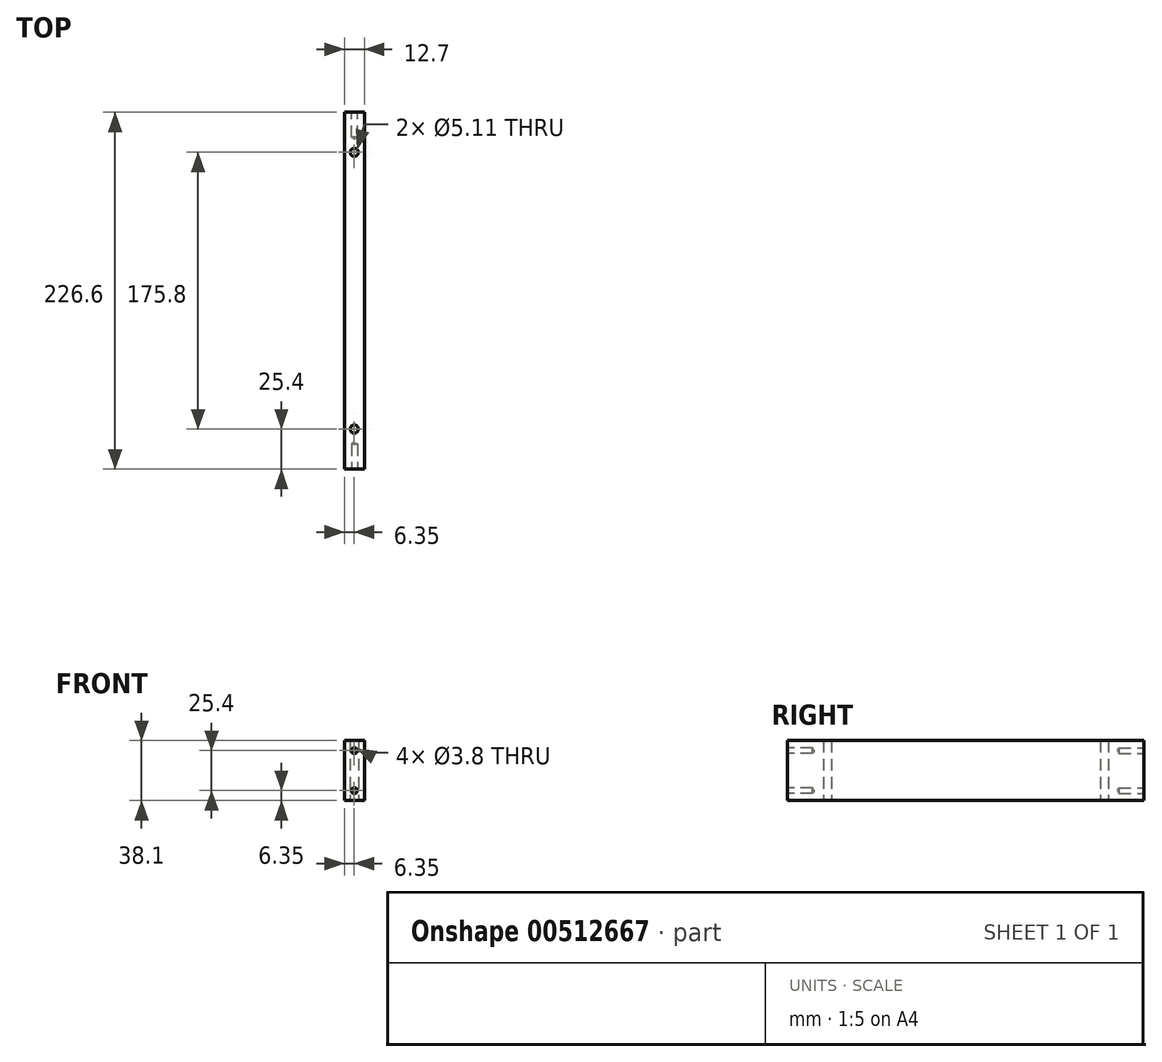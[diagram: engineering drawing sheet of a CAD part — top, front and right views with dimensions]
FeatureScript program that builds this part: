
annotation { "Feature Type Name" : "Feature", "Feature Type Description" : "" }
export const myFeature = defineFeature(function(context is Context, id is Id, definition is map)
    precondition{}
    {
        {
            var Q0;
            Q0=qCreatedBy(makeId("Front.planeOp"),FACE);
            var sketch = newSketch(context, id + "F0", { "sketchPlane" : qUnion([Q0])});
            skLineSegment(sketch, "E0.bottom", {"start": v(0, 0) * mm, "end": v(12.7, 0) * mm});
            skLineSegment(sketch, "E0.top", {"start": v(0, 38.1) * mm, "end": v(12.7, 38.1) * mm});
            skLineSegment(sketch, "E0.left", {"start": v(0, 0) * mm, "end": v(0, 38.1) * mm});
            skLineSegment(sketch, "E0.right", {"start": v(12.7, 0) * mm, "end": v(12.7, 38.1) * mm});
            skSolve(sketch);
        }
        {
            var Q0;
            Q0 = qSketchRegion(id + "F0", true);
            extrude(context, id + "F1", {"entities" : qUnion([Q0]), "depth" : 252 * mm - 25.4 * mm});
        }
        {
            var Q0;
            Q0=makeQuery(id+"F1.opExtrude","CAP_FACE",FACE,{"disambiguationData":[OSD([sQuery(id+"F0.wireOp",EDGE,"E0.bottom"),sQuery(id+"F0.wireOp",EDGE,"E0.top"),sQuery(id+"F0.wireOp",EDGE,"E0.left"),sQuery(id+"F0.wireOp",EDGE,"E0.right")])],"isStart":false});
            var sketch = newSketch(context, id + "F2", { "sketchPlane" : qUnion([Q0])});
            skLineSegment(sketch, "E1", {"start": v(0, 38.1) * mm, "end": v(6.35, 38.1) * mm});
            skLineSegment(sketch, "E2", {"start": v(6.35, 38.1) * mm, "end": v(6.35, 31.75) * mm});
            skLineSegment(sketch, "E3", {"start": v(6.35, 0) * mm, "end": v(6.35, 6.35) * mm});
            skSolve(sketch);
        }
        {
            var Q0;
            Q0=sQuery(id+"F2.wireOp",VERTEX,"E2.end");
            var Q1;
            Q1=sQuery(id+"F2.wireOp",VERTEX,"E3.end");
            var Q2;
            Q2=makeQuery(id+"F1.opExtrude","SWEPT_BODY",BODY,{"disambiguationData":[OSD([sQuery(id+"F0.wireOp",EDGE,"E0.bottom"),sQuery(id+"F0.wireOp",EDGE,"E0.top"),sQuery(id+"F0.wireOp",EDGE,"E0.left"),sQuery(id+"F0.wireOp",EDGE,"E0.right")])]});
            hole(context, id + "F3", {"style" : HoleStyle.SIMPLE, "endStyle" : HoleEndStyle.BLIND, "standardTappedOrClearance" : lookupTablePath({ "standard" : "ANSI", "engagement" : "75%", "pitch" : "24 tpi", "size" : "#10", "type" : "Tapped" }), "standardBlindInLast" : lookupTablePath({ "standard" : "ANSI", "engagement" : "75%", "pitch" : "24 tpi", "size" : "#10", "type" : "Tapped" }), "holeDiameter" : 3.8 * mm, "showTappedDepth" : true, "holeDepth" : 15.88 * mm, "isTappedThrough" : true, "tappedDepth" : 12.7 * mm, "tapClearance" : 3, "locations" : qUnion([Q0, Q1]), "scope" : qUnion([Q2]), "majorDiameter" : 4.83 * mm});
        }
        {
            var Q0;
            Q0=makeQuery(id+"F1.opExtrude","CAP_FACE",FACE,{"disambiguationData":[OSD([sQuery(id+"F0.wireOp",EDGE,"E0.bottom"),sQuery(id+"F0.wireOp",EDGE,"E0.top"),sQuery(id+"F0.wireOp",EDGE,"E0.left"),sQuery(id+"F0.wireOp",EDGE,"E0.right")])],"isStart":true});
            var sketch = newSketch(context, id + "F4", { "sketchPlane" : qUnion([Q0])});
            skLineSegment(sketch, "E4", {"start": v(-6.35, 38.1) * mm, "end": v(-6.35, 31.75) * mm});
            skPoint(sketch, "E4.endSnap0", {"position": v(-6.35, 38.1) * mm});
            skLineSegment(sketch, "E5", {"start": v(-6.35, 0) * mm, "end": v(-6.35, 6.35) * mm});
            skSolve(sketch);
        }
        {
            var Q0;
            Q0=sQuery(id+"F4.wireOp",VERTEX,"E4.end");
            var Q1;
            Q1=sQuery(id+"F4.wireOp",VERTEX,"E5.end");
            var Q2;
            Q2=makeQuery(id+"F1.opExtrude","SWEPT_BODY",BODY,{"disambiguationData":[OSD([sQuery(id+"F0.wireOp",EDGE,"E0.bottom"),sQuery(id+"F0.wireOp",EDGE,"E0.top"),sQuery(id+"F0.wireOp",EDGE,"E0.left"),sQuery(id+"F0.wireOp",EDGE,"E0.right")])]});
            hole(context, id + "F5", {"style" : HoleStyle.SIMPLE, "endStyle" : HoleEndStyle.BLIND, "standardTappedOrClearance" : lookupTablePath({ "standard" : "ANSI", "engagement" : "75%", "pitch" : "24 tpi", "size" : "#10", "type" : "Tapped" }), "standardBlindInLast" : lookupTablePath({ "standard" : "ANSI", "engagement" : "75%", "pitch" : "24 tpi", "size" : "#10", "type" : "Tapped" }), "holeDiameter" : 3.8 * mm, "showTappedDepth" : true, "holeDepth" : 15.88 * mm, "isTappedThrough" : true, "tappedDepth" : 12.7 * mm, "tapClearance" : 3, "locations" : qUnion([Q0, Q1]), "scope" : qUnion([Q2]), "majorDiameter" : 4.83 * mm});
        }
        {
            var Q0;
            Q0=makeQuery(id+"F1.opExtrude","SWEPT_FACE",FACE,{"disambiguationData":[OSD([sQuery(id+"F0.wireOp",EDGE,"E0.bottom")])]});
            var sketch = newSketch(context, id + "F6", { "sketchPlane" : qUnion([Q0])});
            skLineSegment(sketch, "E6", {"start": v(6.35, 226.6) * mm, "end": v(6.35, 201.2) * mm});
            skLineSegment(sketch, "E7", {"start": v(6.35, 0) * mm, "end": v(6.35, 25.4) * mm});
            skSolve(sketch);
        }
        {
            var Q0;
            Q0=sQuery(id+"F6.wireOp",VERTEX,"E7.end");
            var Q1;
            Q1=sQuery(id+"F6.wireOp",VERTEX,"E6.end");
            var Q2;
            Q2=makeQuery(id+"F1.opExtrude","SWEPT_BODY",BODY,{"disambiguationData":[OSD([sQuery(id+"F0.wireOp",EDGE,"E0.bottom"),sQuery(id+"F0.wireOp",EDGE,"E0.top"),sQuery(id+"F0.wireOp",EDGE,"E0.left"),sQuery(id+"F0.wireOp",EDGE,"E0.right")])]});
            hole(context, id + "F7", {"style" : HoleStyle.SIMPLE, "endStyle" : HoleEndStyle.THROUGH, "standardTappedOrClearance" : lookupTablePath({ "standard" : "ANSI", "engagement" : "75%", "pitch" : "20 tpi", "size" : "1/4", "type" : "Tapped" }), "standardBlindInLast" : lookupTablePath({ "standard" : "ANSI", "engagement" : "75%", "pitch" : "20 tpi", "size" : "1/4", "type" : "Tapped" }), "holeDiameter" : 5.1 * mm, "showTappedDepth" : true, "isTappedThrough" : true, "tappedDepth" : 12.7 * mm, "tapClearance" : 3, "locations" : qUnion([Q0, Q1]), "scope" : qUnion([Q2]), "majorDiameter" : 6.35 * mm});
        }
    });
